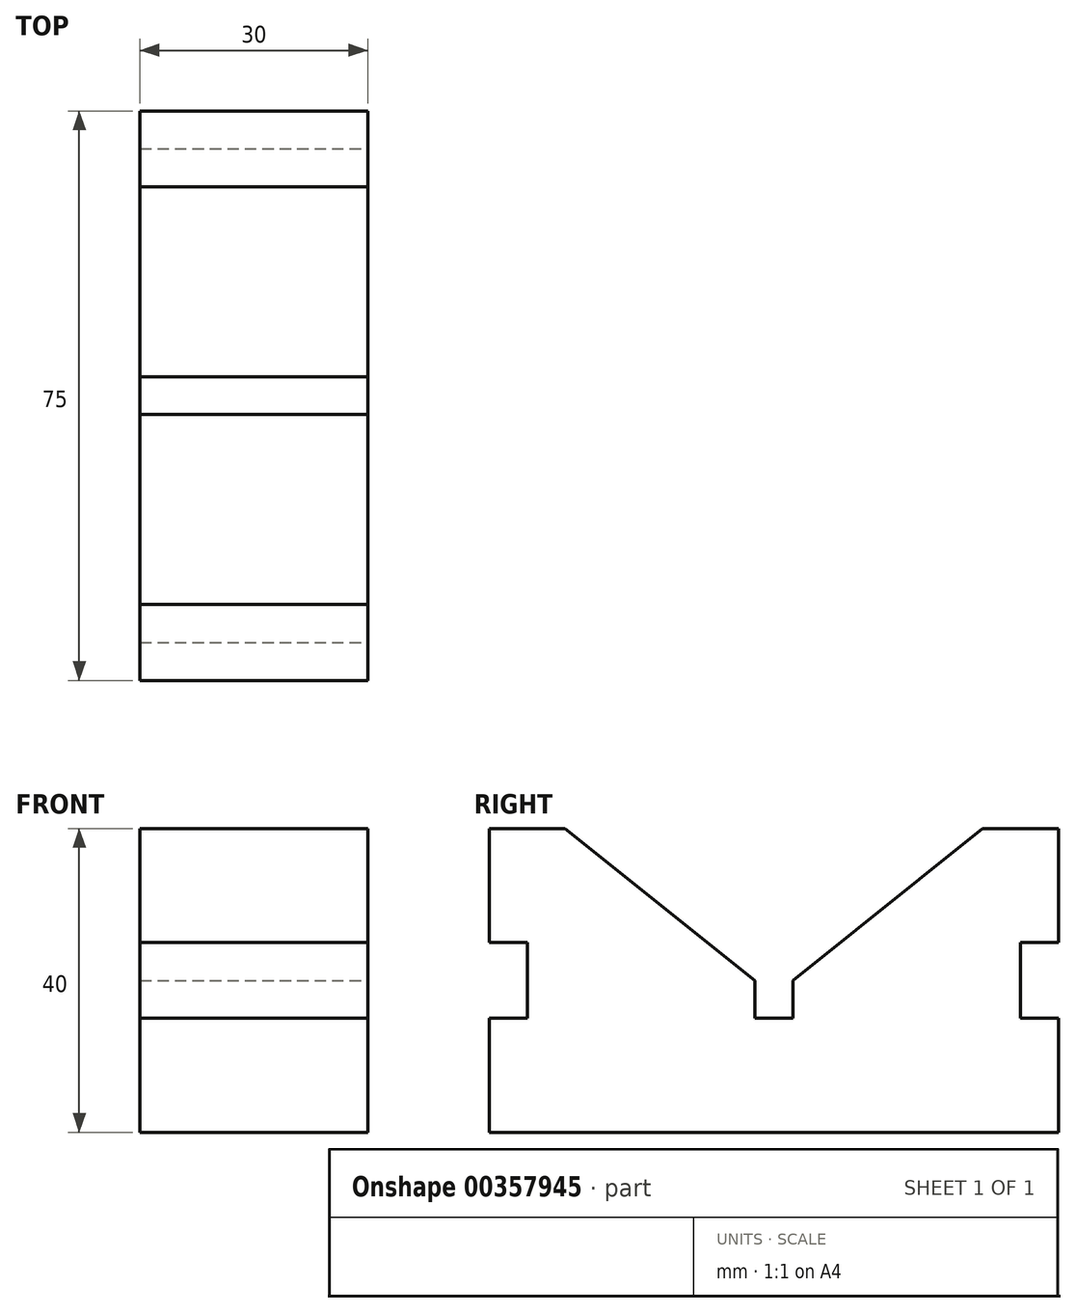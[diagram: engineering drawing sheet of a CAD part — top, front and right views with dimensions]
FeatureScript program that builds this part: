
annotation { "Feature Type Name" : "Feature", "Feature Type Description" : "" }
export const myFeature = defineFeature(function(context is Context, id is Id, definition is map)
    precondition{}
    {
        {
            var Q0;
            Q0=qCreatedBy(makeId("Top.planeOp"),FACE);
            var sketch = newSketch(context, id + "F0", { "sketchPlane" : qUnion([Q0])});
            skLineSegment(sketch, "E0.bottom", {"start": v(-15, 37.5) * mm, "end": v(15, 37.5) * mm});
            skLineSegment(sketch, "E0.top", {"start": v(-15, -37.5) * mm, "end": v(15, -37.5) * mm});
            skLineSegment(sketch, "E0.left", {"start": v(-15, 37.5) * mm, "end": v(-15, -37.5) * mm});
            skLineSegment(sketch, "E0.right", {"start": v(15, 37.5) * mm, "end": v(15, -37.5) * mm});
            skPoint(sketch, "E0.middle", {"position": v(0, 0) * mm});
            skSolve(sketch);
        }
        {
            var Q0;
            Q0 = qSketchRegion(id + "F0", true);
            extrude(context, id + "F1", {"entities" : qUnion([Q0]), "depth" : 40 * mm});
        }
        {
            var Q0;
            Q0=makeQuery(id+"F1.opExtrude","SWEPT_FACE",FACE,{"disambiguationData":[OSD([sQuery(id+"F0.wireOp",EDGE,"E0.right")])]});
            var sketch = newSketch(context, id + "F2", { "sketchPlane" : qUnion([Q0])});
            skLineSegment(sketch, "E1.bottom", {"start": v(-37.5, 25) * mm, "end": v(-32.5, 25) * mm});
            skLineSegment(sketch, "E1.top", {"start": v(-37.5, 15) * mm, "end": v(-32.5, 15) * mm});
            skLineSegment(sketch, "E1.left", {"start": v(-37.5, 25) * mm, "end": v(-37.5, 15) * mm});
            skLineSegment(sketch, "E1.right", {"start": v(-32.5, 25) * mm, "end": v(-32.5, 15) * mm});
            skLineSegment(sketch, "E2.bottom", {"start": v(37.5, 25) * mm, "end": v(32.5, 25) * mm});
            skLineSegment(sketch, "E2.top", {"start": v(37.5, 15) * mm, "end": v(32.5, 15) * mm});
            skLineSegment(sketch, "E2.left", {"start": v(37.5, 25) * mm, "end": v(37.5, 15) * mm});
            skLineSegment(sketch, "E2.right", {"start": v(32.5, 25) * mm, "end": v(32.5, 15) * mm});
            skLineSegment(sketch, "E3.top", {"start": v(-2.5, 15) * mm, "end": v(2.5, 15) * mm});
            skLineSegment(sketch, "E3.left", {"start": v(-2.5, 20) * mm, "end": v(-2.5, 15) * mm});
            skLineSegment(sketch, "E3.right", {"start": v(2.5, 20) * mm, "end": v(2.5, 15) * mm});
            skPoint(sketch, "E3.middle", {"position": v(0, 17.5) * mm});
            skLineSegment(sketch, "E4", {"start": v(-2.5, 20) * mm, "end": v(-27.5, 40) * mm});
            skLineSegment(sketch, "E5", {"start": v(-27.5, 40) * mm, "end": v(27.5, 40) * mm});
            skLineSegment(sketch, "E6", {"start": v(27.5, 40) * mm, "end": v(2.5, 20) * mm});
            skSolve(sketch);
        }
        {
            var Q0;
            Q0 = qSketchRegion(id + "F2", true);
            extrude(context, id + "F3", {"entities" : qUnion([Q0]), "operationType" : NewBodyOperationType.REMOVE, "endBound" : BoundingType.THROUGH_ALL, "oppositeDirection" : true, "depth" : 25 * mm});
        }
    });
